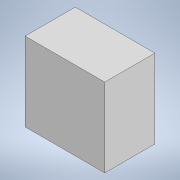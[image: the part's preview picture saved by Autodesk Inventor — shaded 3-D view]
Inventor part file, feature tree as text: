
AUTODESK INVENTOR PART (.ipt)
format: ipt  version: 2021 (Build 250183000, 183)  size: 85,504 bytes
history: native  units: mm
features: extrude x1, sketch x1
ambient origin geometry x8: Origin, YZ Plane, XZ Plane, XY Plane, X Axis, Y Axis, Z Axis, Center Point
bodies: Solid1 (feature_tree)
feature tree (2):
  extrude  "Extrusion1"  Depth=37.3mm
  sketch  "Sketch1"  dims[d0=37.8mm d1=37.3mm d2=23.8mm d3=0.0mm]
